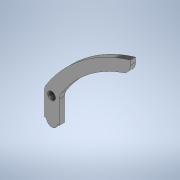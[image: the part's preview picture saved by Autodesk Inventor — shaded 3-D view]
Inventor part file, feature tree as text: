
AUTODESK INVENTOR PART (.ipt)
format: ipt  version: 2021 (Build 250183000, 183)  size: 131,072 bytes
history: native  units: in
note: dims shown in document units (in); Inventor stores cm internally (conversion verified against a paired STEP export)
features: extrude x2, sketch x1, fillet x1
ambient origin geometry x8: Origin, YZ Plane, XZ Plane, XY Plane, X Axis, Y Axis, Z Axis, Center Point
bodies: Solid1 (feature_tree)
feature tree (4):
  sketch  "Sketch1"  dims[d6=0.0591in d9=0.0394in d10=0.0in d11=0.0394in d12=0.0in d28=0.081in d29=0.0157in d30=0.0157in d33=0.5906in d35=0.0787in]
  extrude  "Extrusion1"  Depth=0.0394in TaperAngle=0.0deg
  extrude  "Extrusion2"  Depth=0.0394in TaperAngle=0.0deg
  fillet  "Fillet5"  Radius=0.081in
